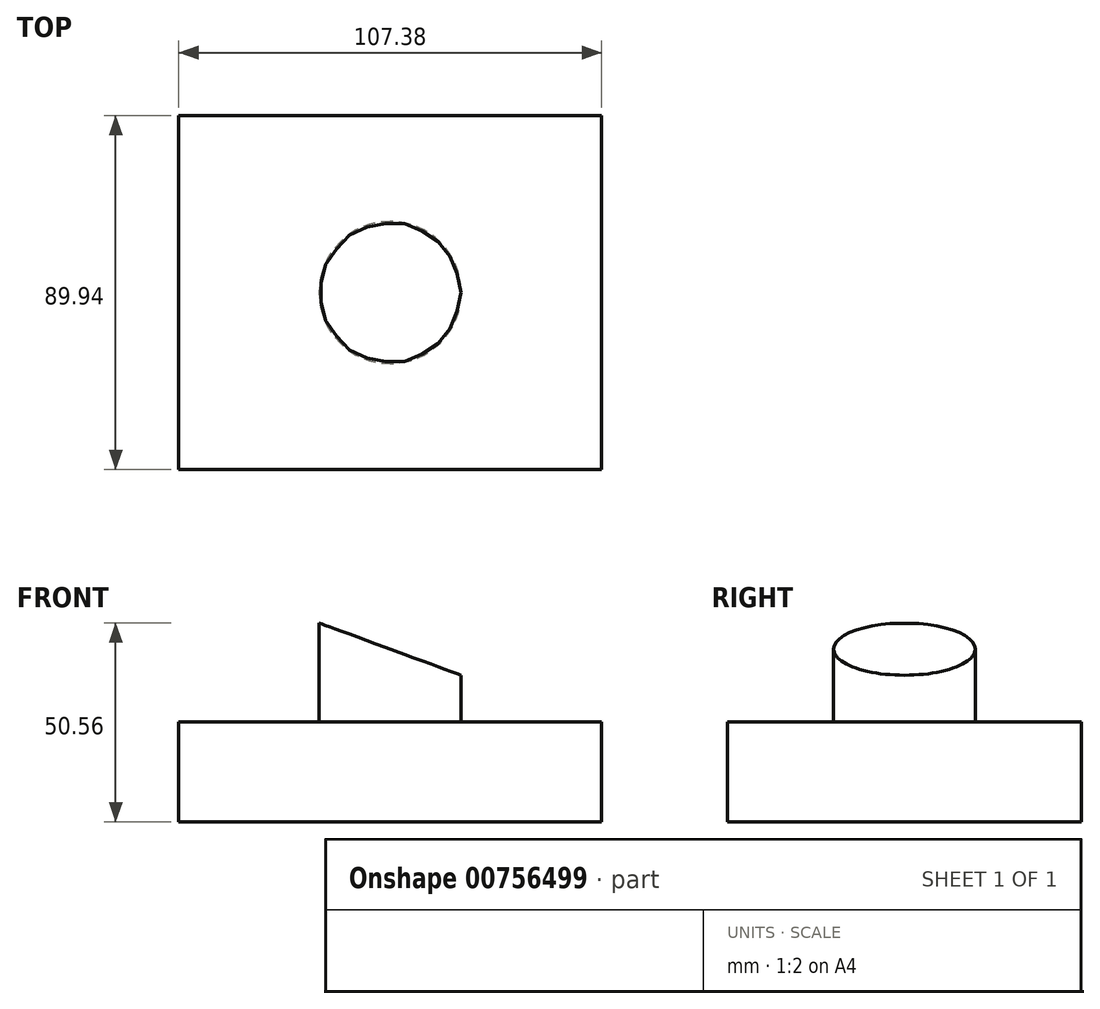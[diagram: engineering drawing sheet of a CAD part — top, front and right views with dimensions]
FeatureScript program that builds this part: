
annotation { "Feature Type Name" : "Feature", "Feature Type Description" : "" }
export const myFeature = defineFeature(function(context is Context, id is Id, definition is map)
    precondition{}
    {
        {
            var Q0;
            Q0=qCreatedBy(makeId("Top.planeOp"),FACE);
            var sketch = newSketch(context, id + "F0", { "sketchPlane" : qUnion([Q0])});
            skLineSegment(sketch, "E0.bottom", {"start": v(53.7, -44.97) * mm, "end": v(-53.7, -44.97) * mm});
            skLineSegment(sketch, "E0.top", {"start": v(53.7, 44.97) * mm, "end": v(-53.7, 44.97) * mm});
            skLineSegment(sketch, "E0.left", {"start": v(53.7, -44.97) * mm, "end": v(53.7, 44.97) * mm});
            skLineSegment(sketch, "E0.right", {"start": v(-53.7, -44.97) * mm, "end": v(-53.7, 44.97) * mm});
            skPoint(sketch, "E0.middle", {"position": v(0, 0) * mm});
            skSolve(sketch);
        }
        {
            var Q0;
            Q0=makeQuery(id+"F0.imprint","IMPRINT",FACE,{"disambiguationData":[TD([[makeQuery(id+"F0.imprint","IMPRINT",EDGE,{"derivedFrom":sQuery(id+"F0.wireOp",EDGE,"E0.bottom")}),-1.0]])]});
            extrude(context, id + "F1", {"entities" : qUnion([Q0]), "depth" : 25.4 * mm, "offsetDistance" : 25.4 * mm});
        }
        {
            var Q0;
            Q0=makeQuery(id+"F1.opExtrude","CAP_FACE",FACE,{"disambiguationData":[OSD([sQuery(id+"F0.wireOp",EDGE,"E0.bottom"),sQuery(id+"F0.wireOp",EDGE,"E0.top"),sQuery(id+"F0.wireOp",EDGE,"E0.left"),sQuery(id+"F0.wireOp",EDGE,"E0.right")])],"isStart":false});
            var sketch = newSketch(context, id + "F2", { "sketchPlane" : qUnion([Q0])});
            skCircle(sketch, "E1", {"center": v(0, 0) * mm, "radius": 18.03 * mm});
            skSolve(sketch);
        }
        {
            var Q0;
            Q0=makeQuery(id+"F2.imprint","IMPRINT",FACE,{"disambiguationData":[TD([[makeQuery(id+"F2.imprint","IMPRINT",EDGE,{"derivedFrom":sQuery(id+"F2.wireOp",EDGE,"E1")}),1.0]])]});
            extrude(context, id + "F3", {"entities" : qUnion([Q0]), "operationType" : NewBodyOperationType.ADD, "depth" : 25.4 * mm, "offsetDistance" : 25.4 * mm});
        }
        {
            var Q0;
            Q0=qCreatedBy(makeId("Front.planeOp"),FACE);
            var sketch = newSketch(context, id + "F4", { "sketchPlane" : qUnion([Q0])});
            skLineSegment(sketch, "E2", {"start": v(-18.7, 50.8) * mm, "end": v(18.28, 37.2) * mm});
            skLineSegment(sketch, "E3", {"start": v(18.28, 37.2) * mm, "end": v(18.28, 50.8) * mm});
            skLineSegment(sketch, "E4", {"start": v(18.28, 50.8) * mm, "end": v(-18.7, 50.8) * mm});
            skSolve(sketch);
        }
        {
            var Q0;
            Q0 = qSketchRegion(id + "F4", true);
            extrude(context, id + "F5", {"entities" : qUnion([Q0]), "operationType" : NewBodyOperationType.REMOVE, "endBound" : BoundingType.THROUGH_ALL, "oppositeDirection" : true, "depth" : 25.4 * mm, "offsetDistance" : 25.4 * mm, "hasSecondDirection" : true, "secondDirectionOppositeDirection" : false, "secondDirectionDepth" : 25.4 * mm});
        }
    });
